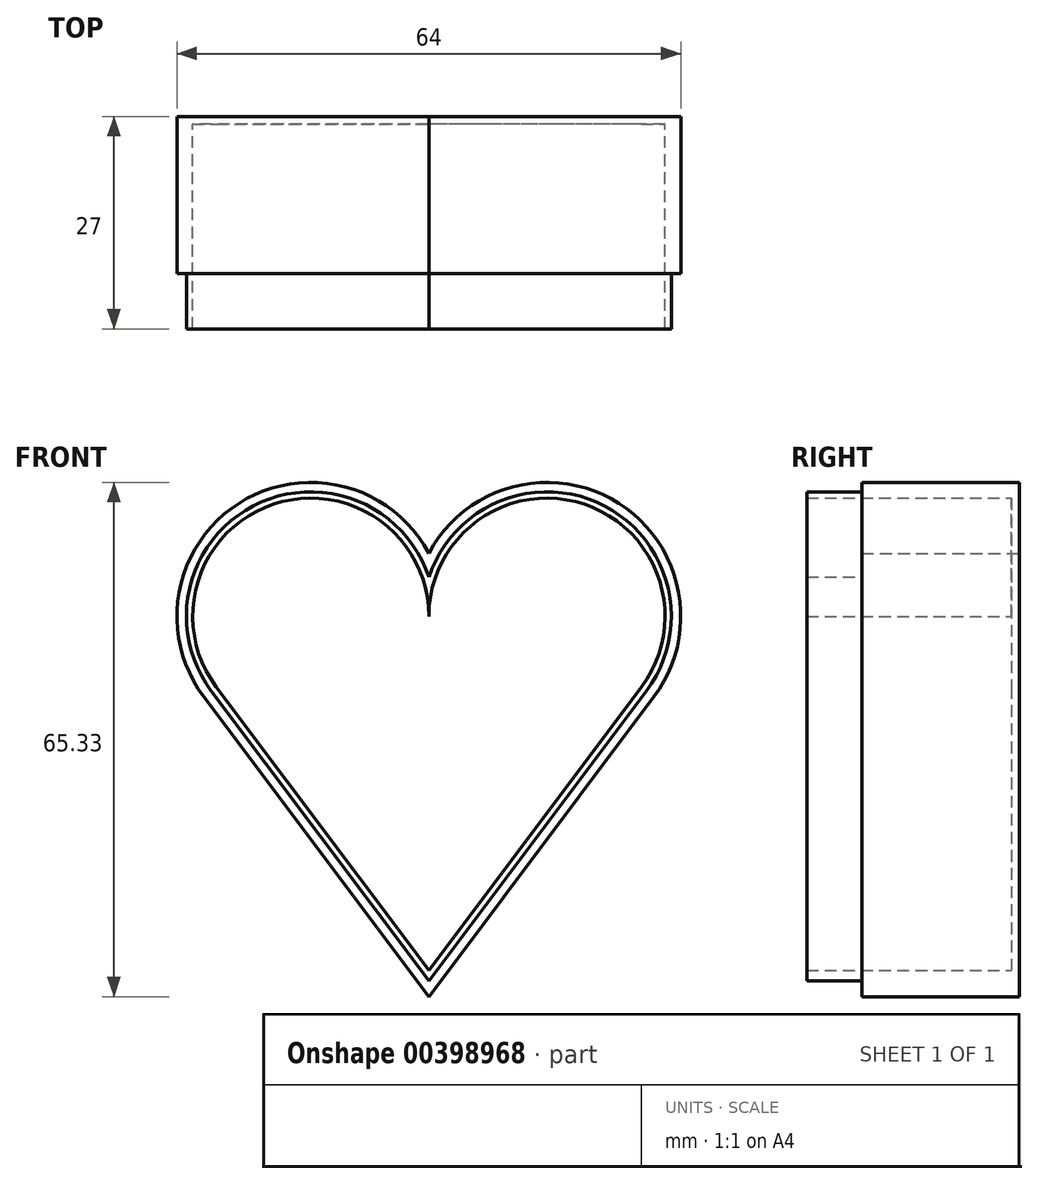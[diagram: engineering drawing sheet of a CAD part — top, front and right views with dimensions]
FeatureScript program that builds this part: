
annotation { "Feature Type Name" : "Feature", "Feature Type Description" : "" }
export const myFeature = defineFeature(function(context is Context, id is Id, definition is map)
    precondition{}
    {
        {
            var Q0;
            Q0=qCreatedBy(makeId("Front.planeOp"),FACE);
            var sketch = newSketch(context, id + "F0", { "sketchPlane" : qUnion([Q0])});
            skArc(sketch, "E0", {"start": v(0, 0) * mm, "mid": v(-19.74, 14.23) * mm, "end": v(-27, -9) * mm});
            skArc(sketch, "E1", {"start": v(27, -9) * mm, "mid": v(19.74, 14.23) * mm, "end": v(0, 0) * mm});
            skLineSegment(sketch, "E2", {"start": v(0, -45) * mm, "end": v(27, -9) * mm});
            skLineSegment(sketch, "E3", {"start": v(0, -45) * mm, "end": v(-27, -9) * mm});
            skPoint(sketch, "E4.start.orphan", {"position": v(0, 0) * mm});
            skArc(sketch, "E5.0", {"start": v(0, 4.96) * mm, "mid": v(-22.32, 14) * mm, "end": v(-27.64, -9.48) * mm});
            skArc(sketch, "E5.1", {"start": v(27.64, -9.48) * mm, "mid": v(22.32, 14) * mm, "end": v(0, 4.96) * mm});
            skLineSegment(sketch, "E5.2", {"start": v(0, -46.33) * mm, "end": v(27.64, -9.48) * mm});
            skLineSegment(sketch, "E5.3", {"start": v(0, -46.33) * mm, "end": v(-27.64, -9.48) * mm});
            skArc(sketch, "E6.0", {"start": v(0, 8) * mm, "mid": v(-24.13, 14.34) * mm, "end": v(-28.6, -10.2) * mm});
            skArc(sketch, "E6.1", {"start": v(28.6, -10.2) * mm, "mid": v(24.13, 14.34) * mm, "end": v(0, 8) * mm});
            skLineSegment(sketch, "E6.2", {"start": v(0, -48.33) * mm, "end": v(28.6, -10.2) * mm});
            skLineSegment(sketch, "E6.3", {"start": v(0, -48.33) * mm, "end": v(-28.6, -10.2) * mm});
            skSolve(sketch);
        }
        {
            var Q0;
            Q0=makeQuery(id+"F0.imprint","IMPRINT",FACE,{"disambiguationData":[TD([[makeQuery(id+"F0.imprint","IMPRINT",EDGE,{"derivedFrom":sQuery(id+"F0.wireOp",EDGE,"E0")}),1.0]])]});
            var Q1;
            Q1=makeQuery(id+"F0.imprint","IMPRINT",FACE,{"disambiguationData":[TD([[makeQuery(id+"F0.imprint","IMPRINT",EDGE,{"derivedFrom":sQuery(id+"F0.wireOp",EDGE,"E0")}),-1.0]])]});
            var Q2;
            Q2=makeQuery(id+"F0.imprint","IMPRINT",FACE,{"disambiguationData":[TD([[makeQuery(id+"F0.imprint","IMPRINT",EDGE,{"derivedFrom":sQuery(id+"F0.wireOp",EDGE,"E5.0")}),-1.0]])]});
            extrude(context, id + "F1", {"entities" : qUnion([Q0, Q1, Q2]), "depth" : 1 * mm});
        }
        {
            var Q0;
            Q0=makeQuery(id+"F0.imprint","IMPRINT",FACE,{"disambiguationData":[TD([[makeQuery(id+"F0.imprint","IMPRINT",EDGE,{"derivedFrom":sQuery(id+"F0.wireOp",EDGE,"E5.0")}),-1.0]])]});
            extrude(context, id + "F2", {"entities" : qUnion([Q0]), "operationType" : NewBodyOperationType.ADD, "depth" : 20 * mm});
        }
        {
            var Q0;
            Q0=makeQuery(id+"F0.imprint","IMPRINT",FACE,{"disambiguationData":[TD([[makeQuery(id+"F0.imprint","IMPRINT",EDGE,{"derivedFrom":sQuery(id+"F0.wireOp",EDGE,"E0")}),-1.0]])]});
            extrude(context, id + "F3", {"entities" : qUnion([Q0]), "operationType" : NewBodyOperationType.ADD, "depth" : 27 * mm});
        }
    });
